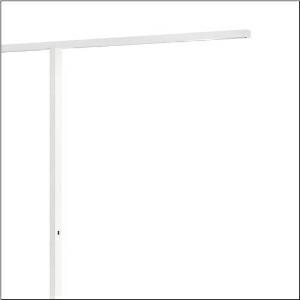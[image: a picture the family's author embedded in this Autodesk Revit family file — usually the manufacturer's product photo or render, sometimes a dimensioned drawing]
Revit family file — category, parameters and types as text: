
# Revit family: silica_r__11_floor_duo_5mx51bs8wzk00006xx_4f95
name_source: partatom
category: Lighting Fixtures
units: mm (PartAtom-declared; Revit-internal decimal feet)

## family parameters
Cut with Voids When Loaded = No
Host = Face
Light Source = No
Part Type = Normal
Room Calculation Point = No
Round Connector Dimension = Use Diameter
Shared = No

## types (1)
- --- (1 x LED, 3970 lm / 8500 lm, 24.1 W / 53.2 W, 4000K)
    Apparent Load = 155 VA
    CIE Flux Codes = 82 97 100 100 100 / - - - 0 100
    Color Rendering = 80
    Color Temperature = 4000K
    Default Elevation = 1800 mm
    Description = Silica® 11 Floor, floorstanding luminaire, of PMMA, primary optical cover: cover panel, of PMMA, light emission: indirect/direct distribution, primary light characteristic: symmetric, installation type: not mounted, LED rated luminous flux: 24.930 lm, light colour: 840, colour temperature: 4000K, control gear: ECG DALI, daylight-dependent control, mains connection: 230V, AC, 50Hz, connection cable pre-assembled, cable length: 3 m, rated input power: 155W, luminaire head, rectangular, rounded, of aluminium, coated, traffic white (RAL 9016), supporting column, angular, of aluminium, coated, traffic white (RAL 9016), baseplate, of steel, coated, traffic white (RAL 9016), length: 2.598 mm, width: 65 mm, protection rating (complete): IP20, insulation class (complete): insulation class I (protective earthing), certification: CE, permissible ambient temperature for indoor applications: 0..+35°C, standard: EN 50419, packaging unit: 1 piece
    Height = 40 mm  [stored 0.131234 ft]
    Lamp = 1 x LED
    Lamp Light Flux = 3970 lm / 8500 lm
    Lamp Power = 24.1 W / 53.2 W
    Lamp count = 1
    Length = 2598 mm
    Luminous efficacy = 161 lm/W
    Manufacturer = Siteco
    ModVariant = No
    Model = 5MX51BS8WZK00006XX
    Mounting Place = Floor
    Mounting Type = Freestanding
    Number of Poles = 1
    OnlyDefault = Yes
    Power Factor = 1
    Product Name = Silica® 11 Floor duo
    Product group = floorstanding luminaire
    ProductGroupID = 1302
    Protection Class = Protection class I
    Protection Degree = IP 20
    RLX_Detail_Level = 1
    RlxData = <blob elided: 19217 chars, md5=f1d0f3a7>
    Socket = socket
    Standby Power = 0 W
    System Light Flux = 24940 lm
    System Power = 155 W
    Type Comments = factory setting: direct and indirect light
    Type Image = l_1004652.jpg
    URL = http://relux.com
    VarID = @adj_133497
    Voltage = 0 V
    Weight = 0.00 kg
    Width = 65 mm

note: [stored X ft] marks values corroborated as IEEE doubles in the binary element streams (Revit-internal decimal feet)

## geometry (parser evidence)
native form markers: Blend x4, Sweep x17
no freeform markers — native parametric forms only
